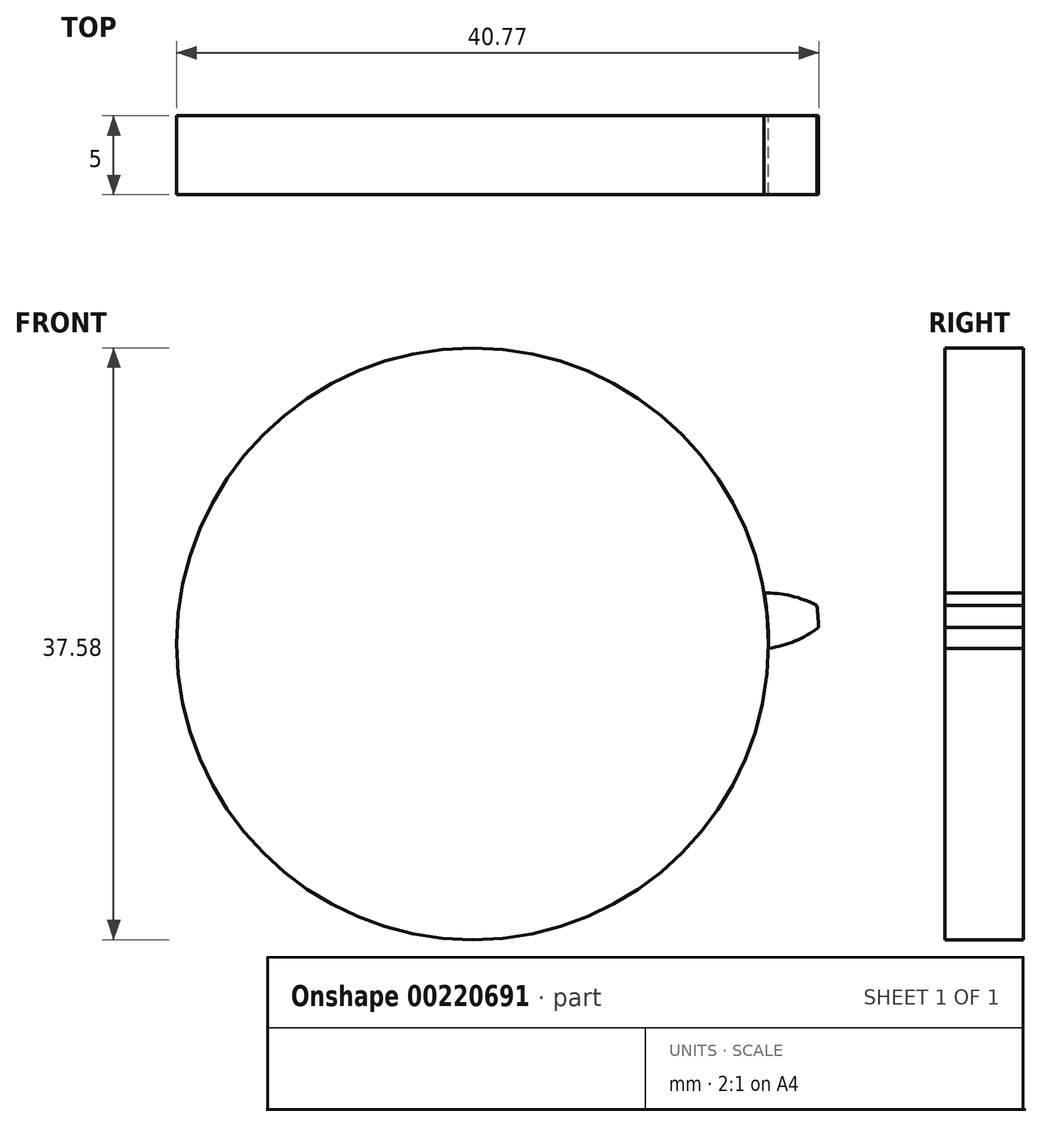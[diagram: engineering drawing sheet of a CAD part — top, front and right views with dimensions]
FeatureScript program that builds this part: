
annotation { "Feature Type Name" : "Feature", "Feature Type Description" : "" }
export const myFeature = defineFeature(function(context is Context, id is Id, definition is map)
    precondition{}
    {
        {
            var Q0;
            Q0=qCreatedBy(makeId("Front.planeOp"),FACE);
            var sketch = newSketch(context, id + "F0", { "sketchPlane" : qUnion([Q0])});
            skCircle(sketch, "E0", {"center": v(0, 0) * mm, "radius": 20 * mm, "construction": true});
            skCircle(sketch, "E1", {"center": v(0, 0) * mm, "radius": 22 * mm, "construction": true});
            skCircle(sketch, "E2", {"center": v(0, 0) * mm, "radius": 18.8 * mm});
            skCircle(sketch, "E3", {"center": v(40, 0) * mm, "radius": 18.8 * mm, "construction": true});
            skLineSegment(sketch, "E4", {"start": v(17.66, 6.43) * mm, "end": v(20, 0) * mm, "construction": true});
            skLineSegment(sketch, "E5", {"start": v(0, 0) * mm, "end": v(20, 0) * mm, "construction": true});
            skLineSegment(sketch, "E6", {"start": v(20, 0) * mm, "end": v(20, 28.46) * mm, "construction": true});
            skLineSegment(sketch, "E7", {"start": v(20, 0) * mm, "end": v(22.34, -6.43) * mm, "construction": true});
            skLineSegment(sketch, "E8", {"start": v(20, 0) * mm, "end": v(40, 0) * mm, "construction": true});
            skLineSegment(sketch, "E9", {"start": v(17.66, 6.43) * mm, "end": v(0, 0) * mm, "construction": true});
            skArc(sketch, "E10", {"start": v(17.66, 6.43) * mm, "mid": v(18.53, 3.13) * mm, "end": v(18.8, -0.28) * mm, "construction": true});
            skArc(sketch, "E11", {"start": v(18.8, -0.28) * mm, "mid": v(18.01, 5.36) * mm, "end": v(15.58, 10.51) * mm, "construction": true});
            skLineSegment(sketch, "E12", {"start": v(15.58, 10.51) * mm, "end": v(0, 0) * mm, "construction": true});
            skLineSegment(sketch, "E13", {"start": v(15.58, 10.51) * mm, "end": v(21.98, 1.03) * mm, "construction": true});
            skLineSegment(sketch, "E14", {"start": v(18.8, -0.28) * mm, "end": v(0, 0) * mm, "construction": true});
            skArc(sketch, "E15", {"start": v(18.8, -0.28) * mm, "mid": v(20.47, 0.17) * mm, "end": v(21.98, 1.03) * mm});
            skLineSegment(sketch, "E16", {"start": v(0, 0) * mm, "end": v(21.93, 1.73) * mm, "construction": true});
            skArc(sketch, "E17.MirrorCS", {"start": v(18.51, 3.23) * mm, "mid": v(20.24, 3.04) * mm, "end": v(21.87, 2.43) * mm});
            skPoint(sketch, "E18", {"position": v(19.75, 3.14) * mm});
            skArc(sketch, "E19", {"start": v(21.98, 1.03) * mm, "mid": v(21.93, 1.73) * mm, "end": v(21.87, 2.43) * mm});
            skPoint(sketch, "E20", {"position": v(18.74, 1.48) * mm});
            skArc(sketch, "E21", {"start": v(18.8, -0.28) * mm, "mid": v(18.74, 1.48) * mm, "end": v(18.51, 3.23) * mm});
            skSolve(sketch);
        }
        {
            var Q0;
            {var subQ0=sQuery(id+"F0.wireOp",EDGE,"E2");var subQ1=makeQuery(id+"F0.imprint","INTERSECT",VERTEX,{"derivedFrom":[subQ0,sQuery(id+"F0.wireOp",EDGE,"E15")]});Q0=makeQuery(id+"F0.imprint","IMPRINT",FACE,{"disambiguationData":[TD([[makeQuery(id+"F0.imprint","IMPRINT",EDGE,{"disambiguationData":[TD([[subQ1,1.0]])],"derivedFrom":subQ0}),1.0]])]});}
            extrude(context, id + "F1", {"entities" : qUnion([Q0]), "depth" : 5 * mm});
        }
        {
            var Q0;
            {var subQ0=sQuery(id+"F0.wireOp",EDGE,"E15");Q0=makeQuery(id+"F0.imprint","IMPRINT",FACE,{"disambiguationData":[TD([[makeQuery(id+"F0.imprint","IMPRINT",EDGE,{"derivedFrom":subQ0}),1.0]])]});}
            extrude(context, id + "F2", {"entities" : qUnion([Q0]), "depth" : 5 * mm});
        }
    });
